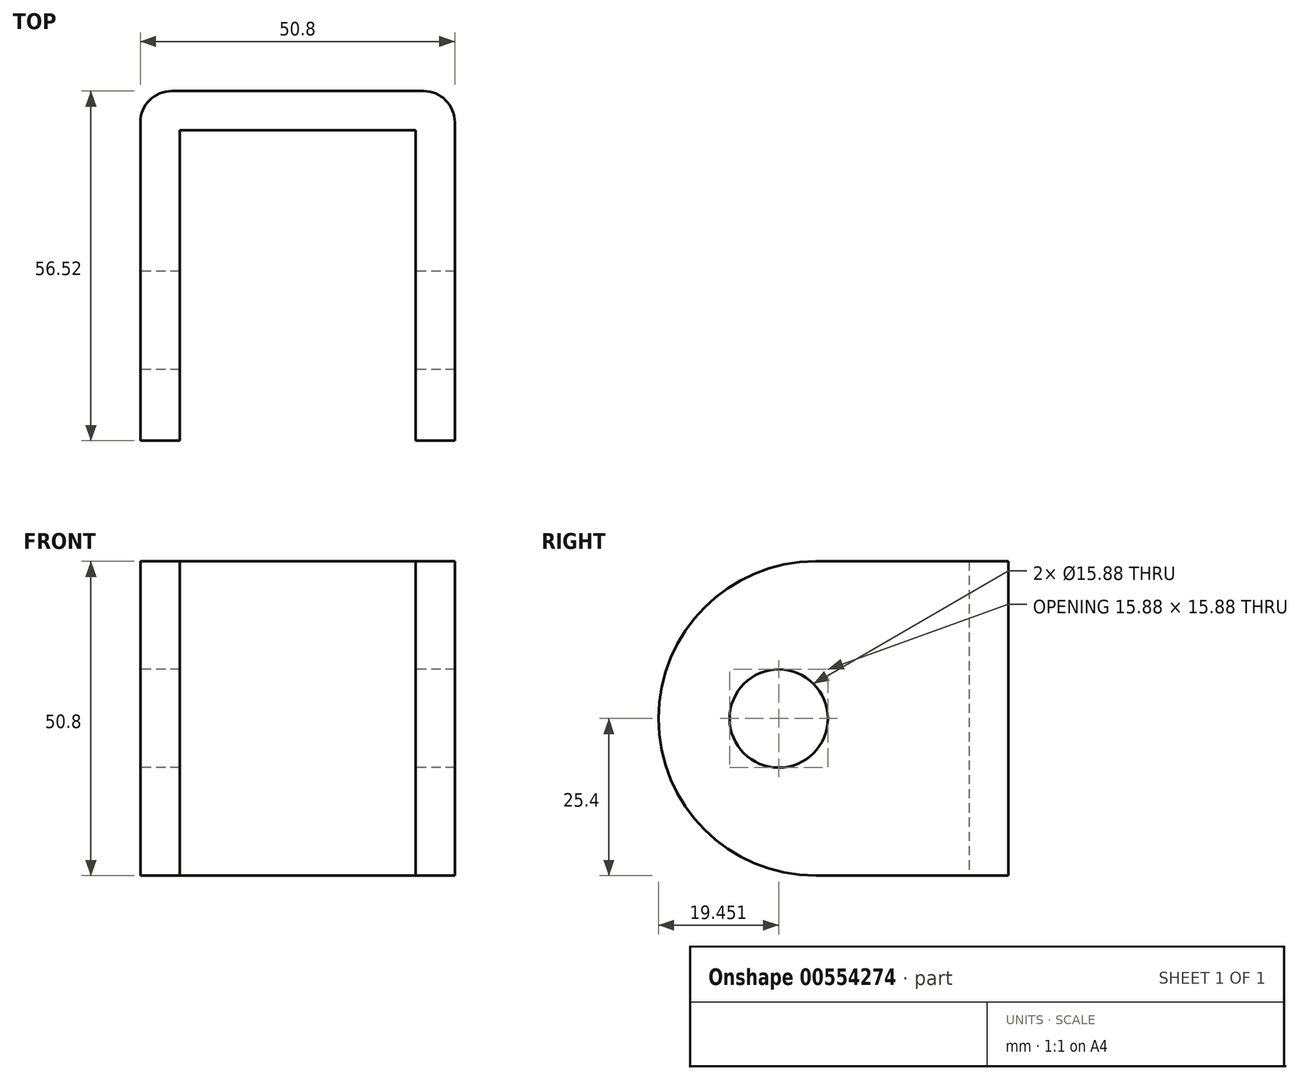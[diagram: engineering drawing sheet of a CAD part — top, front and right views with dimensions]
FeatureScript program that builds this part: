
annotation { "Feature Type Name" : "Feature", "Feature Type Description" : "" }
export const myFeature = defineFeature(function(context is Context, id is Id, definition is map)
    precondition{}
    {
        {
            var Q0;
            Q0=qCreatedBy(makeId("Front.planeOp"),FACE);
            var sketch = newSketch(context, id + "F0", { "sketchPlane" : qUnion([Q0])});
            skLineSegment(sketch, "E0.bottom", {"start": v(0, 0) * mm, "end": v(-50.8, 0) * mm});
            skLineSegment(sketch, "E0.top", {"start": v(0, 50.8) * mm, "end": v(-50.8, 50.8) * mm});
            skLineSegment(sketch, "E0.left", {"start": v(0, 0) * mm, "end": v(0, 50.8) * mm});
            skLineSegment(sketch, "E0.right", {"start": v(-50.8, 0) * mm, "end": v(-50.8, 50.8) * mm});
            skSolve(sketch);
        }
        {
            var Q0;
            Q0 = qSketchRegion(id + "F0", true);
            extrude(context, id + "F1", {"entities" : qUnion([Q0]), "depth" : 6.35 * mm, "offsetDistance" : 25.4 * mm});
        }
        {
            var Q0;
            Q0=makeQuery(id+"F1.opExtrude","CAP_FACE",FACE,{"disambiguationData":[OSD([sQuery(id+"F0.wireOp",EDGE,"E0.bottom"),sQuery(id+"F0.wireOp",EDGE,"E0.top"),sQuery(id+"F0.wireOp",EDGE,"E0.left"),sQuery(id+"F0.wireOp",EDGE,"E0.right")])],"isStart":false});
            var sketch = newSketch(context, id + "F2", { "sketchPlane" : qUnion([Q0])});
            skLineSegment(sketch, "E1", {"start": v(-50.8, 50.8) * mm, "end": v(-44.44, 50.8) * mm});
            skLineSegment(sketch, "E2", {"start": v(-44.44, 50.8) * mm, "end": v(-44.44, 0) * mm});
            skLineSegment(sketch, "E3", {"start": v(0, 50.8) * mm, "end": v(-6.35, 50.8) * mm});
            skLineSegment(sketch, "E4", {"start": v(-6.35, 50.8) * mm, "end": v(-6.35, 0) * mm});
            skSolve(sketch);
        }
        {
            var Q0;
            Q0 = qSketchRegion(id + "F2", true);
            var Q1;
            Q1=makeQuery(id+"F2.imprint","IMPRINT",FACE,{"disambiguationData":[TD([[makeQuery(id+"F2.imprint","IMPRINT",EDGE,{"derivedFrom":sQuery(id+"F2.wireOp",EDGE,"E1")}),1.0]])]});
            var Q2;
            Q2=makeQuery(id+"F2.imprint","IMPRINT",FACE,{"disambiguationData":[TD([[makeQuery(id+"F2.imprint","IMPRINT",EDGE,{"derivedFrom":sQuery(id+"F2.wireOp",EDGE,"E3")}),1.0]])]});
            extrude(context, id + "F3", {"entities" : qUnion([Q0, Q1, Q2]), "operationType" : NewBodyOperationType.ADD, "depth" : 44.45 * mm, "offsetDistance" : 25.4 * mm});
        }
        {
            var Q0;
            Q0=makeQuery(id+"F3.opExtrude","CAP_EDGE",EDGE,{"disambiguationData":[OSD([sQuery(id+"F2.wireOp",EDGE,"E4")])],"isStart":true});
            var Q1;
            Q1=makeQuery(id+"F1.opExtrude","CAP_EDGE",EDGE,{"disambiguationData":[OSD([sQuery(id+"F0.wireOp",EDGE,"E0.right")])],"isStart":true});
            var Q2;
            Q2=makeQuery(id+"F3.opExtrude","CAP_EDGE",EDGE,{"disambiguationData":[OSD([sQuery(id+"F2.wireOp",EDGE,"E2")])],"isStart":true});
            var Q3;
            Q3=makeQuery(id+"F1.opExtrude","CAP_EDGE",EDGE,{"disambiguationData":[OSD([sQuery(id+"F0.wireOp",EDGE,"E0.left")])],"isStart":true});
            fillet(context, id + "F4", {"entities" : qUnion([Q0, Q1, Q2, Q3]), "radius" : 5.08 * mm, "tangentPropagation" : true, "allowEdgeOverflow" : false});
        }
        {
            var Q0;
            Q0=makeQuery(id+"F3.opExtrude","CAP_FACE",FACE,{"disambiguationData":[OSD([sQuery(id+"F0.wireOp",EDGE,"E0.bottom"),sQuery(id+"F0.wireOp",EDGE,"E0.right"),sQuery(id+"F2.wireOp",EDGE,"E1"),sQuery(id+"F2.wireOp",EDGE,"E2")])],"isStart":false});
            var Q1;
            Q1=makeQuery(id+"F3.opExtrude","CAP_FACE",FACE,{"disambiguationData":[OSD([sQuery(id+"F0.wireOp",EDGE,"E0.bottom"),sQuery(id+"F0.wireOp",EDGE,"E0.left"),sQuery(id+"F2.wireOp",EDGE,"E3"),sQuery(id+"F2.wireOp",EDGE,"E4")])],"isStart":false});
            extrude(context, id + "F5", {"entities" : qUnion([Q0, Q1]), "operationType" : NewBodyOperationType.ADD, "depth" : 6.35 * mm, "offsetDistance" : 25.4 * mm});
        }
        {
            var Q0;
            {var subQ0=sQuery(id+"F0.wireOp",EDGE,"E0.right");Q0=makeQuery(id+"F5.boolean.opBoolean","MERGE",FACE,{"derivedFrom":[makeQuery(id+"F3.boolean.opBoolean","MERGE",FACE,{"derivedFrom":[makeQuery(id+"F1.opExtrude","SWEPT_FACE",FACE,{"disambiguationData":[OSD([subQ0])]}),makeQuery(id+"F3.opExtrude","SWEPT_FACE",FACE,{"disambiguationData":[OSD([subQ0])]})]}),makeQuery(id+"F5.opExtrude","SWEPT_FACE",FACE,{"disambiguationData":[OSD([subQ0])]})]});}
            var sketch = newSketch(context, id + "F6", { "sketchPlane" : qUnion([Q0])});
            skCircle(sketch, "E5", {"center": v(31.11, 25.4) * mm, "radius": 25.4 * mm});
            skPoint(sketch, "E5.centerSnap0", {"position": v(57.15, 25.4) * mm});
            skPoint(sketch, "E5.centerSnap1", {"position": v(31.11, 50.8) * mm});
            skSolve(sketch);
        }
        {
            var Q0;
            {var subQ1=sQuery(id+"F0.wireOp",EDGE,"E0.right");var subQ8=makeQuery(id+"F5.opExtrude","CAP_EDGE",EDGE,{"disambiguationData":[OSD([subQ1])],"isStart":false});Q0=makeQuery(id+"F6.imprint","IMPRINT",FACE,{"disambiguationData":[TD([[makeQuery(id+"F6.imprint","IMPRINT",EDGE,{"derivedFrom":subQ8}),1.0]])]});}
            extrude(context, id + "F7", {"entities" : qUnion([Q0]), "operationType" : NewBodyOperationType.REMOVE, "oppositeDirection" : true, "depth" : 148.34 * mm, "offsetDistance" : 25.4 * mm});
        }
        {
            var Q0;
            {var subQ0=sQuery(id+"F0.wireOp",EDGE,"E0.right");Q0=makeQuery(id+"F5.boolean.opBoolean","MERGE",FACE,{"derivedFrom":[makeQuery(id+"F3.boolean.opBoolean","MERGE",FACE,{"derivedFrom":[makeQuery(id+"F1.opExtrude","SWEPT_FACE",FACE,{"disambiguationData":[OSD([subQ0])]}),makeQuery(id+"F3.opExtrude","SWEPT_FACE",FACE,{"disambiguationData":[OSD([subQ0])]})]}),makeQuery(id+"F5.opExtrude","SWEPT_FACE",FACE,{"disambiguationData":[OSD([subQ0])]})]});}
            var sketch = newSketch(context, id + "F8", { "sketchPlane" : qUnion([Q0])});
            skCircle(sketch, "E6", {"center": v(37.07, 25.4) * mm, "radius": 7.94 * mm});
            skPoint(sketch, "E6.centerSnap0", {"position": v(56.51, 25.4) * mm});
            skSolve(sketch);
        }
        {
            var Q0;
            Q0=makeQuery(id+"F8.imprint","IMPRINT",FACE,{"disambiguationData":[TD([[makeQuery(id+"F8.imprint","IMPRINT",EDGE,{"derivedFrom":sQuery(id+"F8.wireOp",EDGE,"E6")}),1.0]])]});
            extrude(context, id + "F9", {"entities" : qUnion([Q0]), "operationType" : NewBodyOperationType.REMOVE, "oppositeDirection" : true, "depth" : 94.74 * mm, "offsetDistance" : 25.4 * mm});
        }
    });
